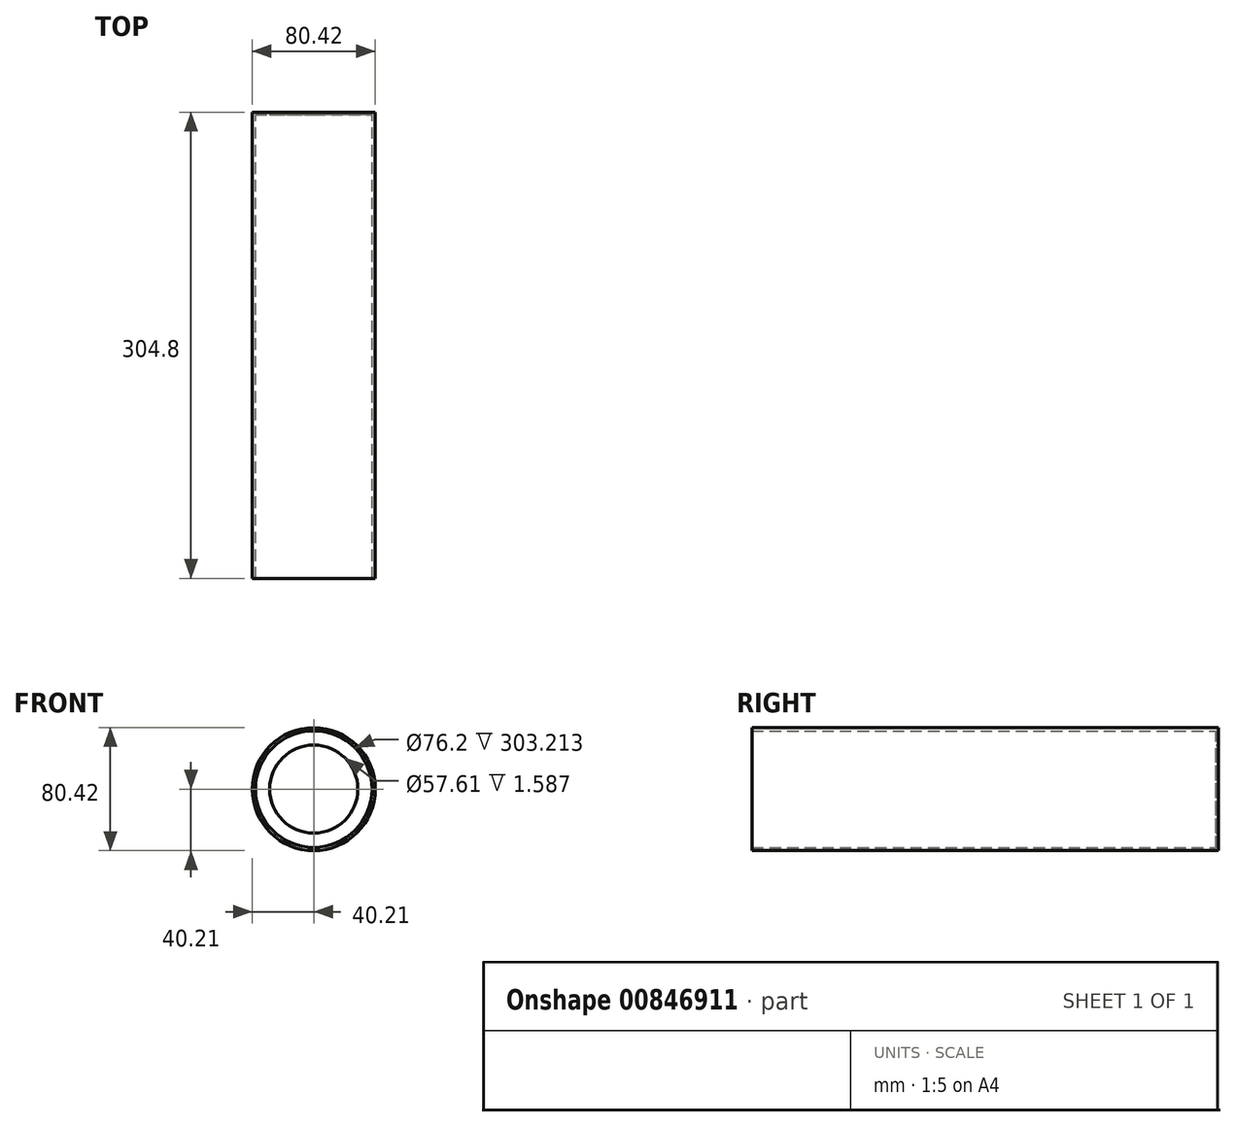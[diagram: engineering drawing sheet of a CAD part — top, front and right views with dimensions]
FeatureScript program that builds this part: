
annotation { "Feature Type Name" : "Feature", "Feature Type Description" : "" }
export const myFeature = defineFeature(function(context is Context, id is Id, definition is map)
    precondition{}
    {
        {
            var Q0;
            Q0=qCreatedBy(makeId("Front.planeOp"),FACE);
            var sketch = newSketch(context, id + "F0", { "sketchPlane" : qUnion([Q0])});
            skCircle(sketch, "E0", {"center": v(0, 0) * mm, "radius": 40.2 * mm});
            skCircle(sketch, "E1", {"center": v(0, 0) * mm, "radius": 42.75 * mm});
            skCircle(sketch, "E2", {"center": v(0, 0) * mm, "radius": 38.1 * mm});
            skCircle(sketch, "E3", {"center": v(0, 0) * mm, "radius": 28.8 * mm});
            skSolve(sketch);
        }
        {
            var Q0;
            Q0=makeQuery(id+"F0.imprint","IMPRINT",FACE,{"disambiguationData":[TD([[makeQuery(id+"F0.imprint","IMPRINT",EDGE,{"derivedFrom":sQuery(id+"F0.wireOp",EDGE,"E0")}),1.0]])]});
            extrude(context, id + "F1", {"entities" : qUnion([Q0]), "depth" : 304.8 * mm, "offsetDistance" : 25.4 * mm});
        }
        {
            var Q0;
            Q0=qCreatedBy(makeId("Front.planeOp"),FACE);
            cPlane(context, id + "F2", {"entities" : qUnion([Q0]), "cplaneType" : CPlaneType.OFFSET, "offset" : 301.62 * mm, "width" : 152.4 * mm, "height" : 152.4 * mm});
        }
        {
            var Q0;
            Q0=qCreatedBy(makeId("Right.planeOp"),FACE);
            var sketch = newSketch(context, id + "F3", { "sketchPlane" : qUnion([Q0])});
            skCircle(sketch, "E4", {"center": v(-285.75, 0) * mm, "radius": 8.46 * mm});
            skCircle(sketch, "E5", {"center": v(-19.05, 0) * mm, "radius": 8.46 * mm});
            skCircle(sketch, "E6", {"center": v(-19.05, 0) * mm, "radius": 6.35 * mm});
            skCircle(sketch, "E7", {"center": v(-285.75, 0) * mm, "radius": 6.35 * mm});
            skSolve(sketch);
        }
        {
            var Q0;
            Q0=makeQuery(id+"F0.imprint","IMPRINT",FACE,{"disambiguationData":[TD([[makeQuery(id+"F0.imprint","IMPRINT",EDGE,{"derivedFrom":sQuery(id+"F0.wireOp",EDGE,"E2")}),1.0]])]});
            extrude(context, id + "F4", {"entities" : qUnion([Q0]), "operationType" : NewBodyOperationType.ADD, "depth" : 1.59 * mm, "offsetDistance" : 25.4 * mm});
        }
    });
